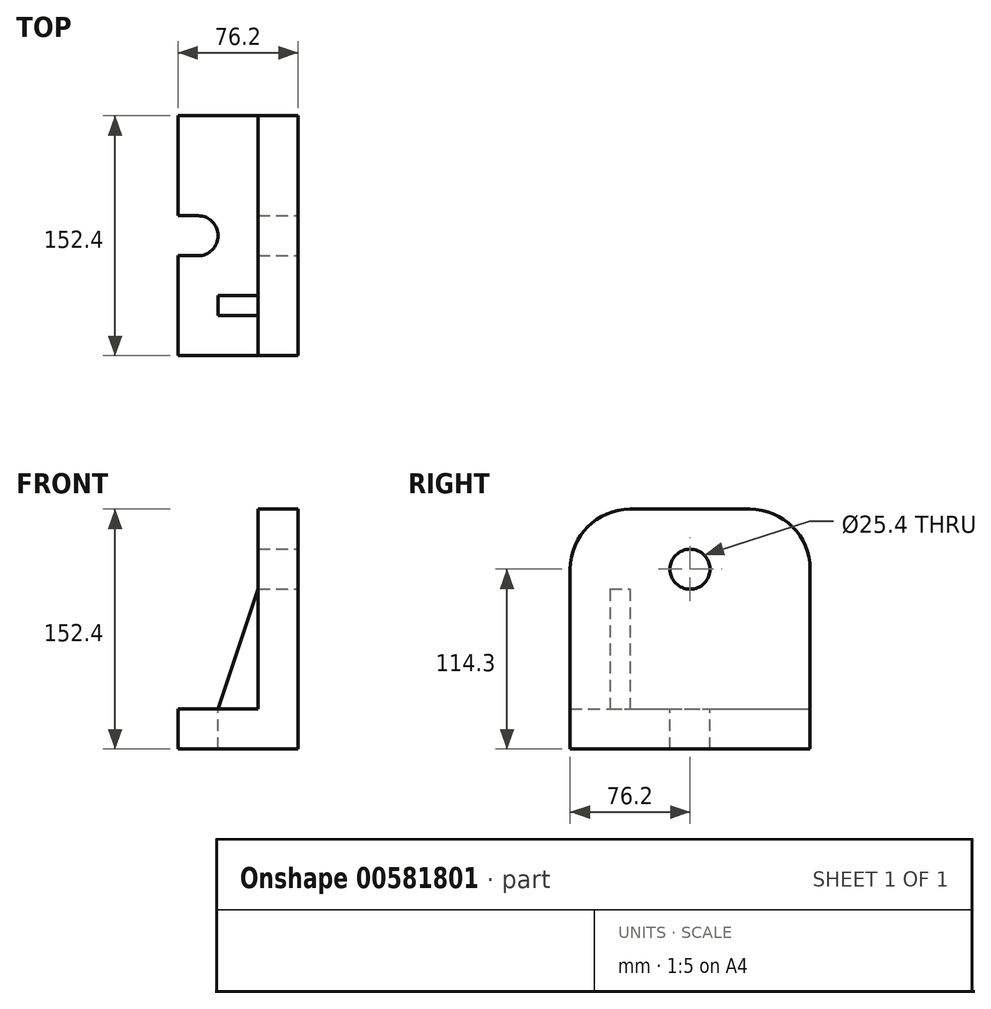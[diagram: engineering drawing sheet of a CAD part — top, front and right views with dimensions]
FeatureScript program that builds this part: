
annotation { "Feature Type Name" : "Feature", "Feature Type Description" : "" }
export const myFeature = defineFeature(function(context is Context, id is Id, definition is map)
    precondition{}
    {
        {
            var Q0;
            Q0=qCreatedBy(makeId("Front.planeOp"),FACE);
            var sketch = newSketch(context, id + "F0", { "sketchPlane" : qUnion([Q0])});
            skLineSegment(sketch, "E0", {"start": v(0, 0) * mm, "end": v(0, 152.4) * mm});
            skLineSegment(sketch, "E1", {"start": v(0, 152.4) * mm, "end": v(-25.4, 152.4) * mm});
            skLineSegment(sketch, "E2", {"start": v(-25.4, 152.4) * mm, "end": v(-25.4, 25.4) * mm});
            skLineSegment(sketch, "E3", {"start": v(-25.4, 25.4) * mm, "end": v(-76.2, 25.4) * mm});
            skLineSegment(sketch, "E4", {"start": v(-76.2, 25.4) * mm, "end": v(-76.2, 0) * mm});
            skLineSegment(sketch, "E5", {"start": v(-76.2, 0) * mm, "end": v(0, 0) * mm});
            skSolve(sketch);
        }
        {
            var Q0;
            Q0 = qSketchRegion(id + "F0", true);
            extrude(context, id + "F1", {"entities" : qUnion([Q0]), "endBound" : BoundingType.SYMMETRIC, "depth" : 152.4 * mm, "offsetDistance" : 25.4 * mm});
        }
        {
            var Q0;
            Q0=qCreatedBy(makeId("Right.planeOp"),FACE);
            var sketch = newSketch(context, id + "F2", { "sketchPlane" : qUnion([Q0])});
            skCircle(sketch, "E6", {"center": v(0, 114.3) * mm, "radius": 12.7 * mm});
            skSolve(sketch);
        }
        {
            var Q0;
            Q0 = qSketchRegion(id + "F2", true);
            extrude(context, id + "F3", {"entities" : qUnion([Q0]), "operationType" : NewBodyOperationType.REMOVE, "endBound" : BoundingType.THROUGH_ALL, "oppositeDirection" : true, "depth" : 25.4 * mm, "offsetDistance" : 25.4 * mm});
        }
        {
            var Q0;
            Q0=makeQuery(id+"F1.opExtrude","SWEPT_FACE",FACE,{"disambiguationData":[OSD([sQuery(id+"F0.wireOp",EDGE,"E3")])]});
            var sketch = newSketch(context, id + "F4", { "sketchPlane" : qUnion([Q0])});
            skLineSegment(sketch, "E7", {"start": v(-76.2, 0) * mm, "end": v(-76.2, 12.7) * mm});
            skLineSegment(sketch, "E8", {"start": v(-76.2, 12.7) * mm, "end": v(-63.5, 12.7) * mm});
            skLineSegment(sketch, "E9.MirrorCS", {"start": v(-76.2, 0) * mm, "end": v(-76.2, -12.7) * mm});
            skLineSegment(sketch, "E10.MirrorCS", {"start": v(-76.2, -12.7) * mm, "end": v(-63.5, -12.7) * mm});
            skArc(sketch, "E11", {"start": v(-63.5, 12.7) * mm, "mid": v(-50.8, 0) * mm, "end": v(-63.5, -12.7) * mm});
            skPoint(sketch, "E12.orphan", {"position": v(-25.4, 0) * mm});
            skSolve(sketch);
        }
        {
            var Q0;
            Q0=makeQuery(id+"F4.imprint","IMPRINT",FACE,{"disambiguationData":[TD([[makeQuery(id+"F4.imprint","IMPRINT",EDGE,{"derivedFrom":sQuery(id+"F4.wireOp",EDGE,"E7")}),-1.0]])]});
            extrude(context, id + "F5", {"entities" : qUnion([Q0]), "operationType" : NewBodyOperationType.REMOVE, "endBound" : BoundingType.THROUGH_ALL, "oppositeDirection" : true, "depth" : 25.4 * mm, "offsetDistance" : 25.4 * mm});
        }
        {
            var Q0;
            Q0=makeQuery(id+"F1.opExtrude","CAP_EDGE",EDGE,{"disambiguationData":[OSD([sQuery(id+"F0.wireOp",EDGE,"E1")])],"isStart":false});
            var Q1;
            Q1=makeQuery(id+"F1.opExtrude","CAP_EDGE",EDGE,{"disambiguationData":[OSD([sQuery(id+"F0.wireOp",EDGE,"E1")])],"isStart":true});
            fillet(context, id + "F6", {"entities" : qUnion([Q0, Q1]), "radius" : 38.1 * mm, "tangentPropagation" : true, "allowEdgeOverflow" : false});
        }
        {
            var Q0;
            Q0=qCreatedBy(makeId("Front.planeOp"),FACE);
            cPlane(context, id + "F7", {"entities" : qUnion([Q0]), "cplaneType" : CPlaneType.OFFSET, "offset" : 44.45 * mm, "width" : 152.4 * mm, "height" : 152.4 * mm});
        }
        {
            var Q0;
            Q0=qCreatedBy(id+"F7.planeOp",FACE);
            var sketch = newSketch(context, id + "F8", { "sketchPlane" : qUnion([Q0])});
            skLineSegment(sketch, "E13.0", {"start": v(-25.4, 25.4) * mm, "end": v(-50.8, 25.4) * mm});
            skLineSegment(sketch, "E14.0", {"start": v(-25.4, 101.6) * mm, "end": v(-25.4, 25.4) * mm});
            skLineSegment(sketch, "E15", {"start": v(-25.4, 25.4) * mm, "end": v(-25.4, 101.6) * mm});
            skLineSegment(sketch, "E16", {"start": v(-76.2, 25.4) * mm, "end": v(-50.8, 25.4) * mm});
            skLineSegment(sketch, "E17", {"start": v(-25.4, 101.6) * mm, "end": v(-50.8, 25.4) * mm});
            skPoint(sketch, "E18.orphan", {"position": v(-25.4, 114.3) * mm});
            skSolve(sketch);
        }
        {
            var Q0;
            Q0 = qSketchRegion(id + "F8", true);
            extrude(context, id + "F9", {"entities" : qUnion([Q0]), "operationType" : NewBodyOperationType.ADD, "endBound" : BoundingType.SYMMETRIC, "depth" : 12.7 * mm, "offsetDistance" : 25.4 * mm});
        }
    });
